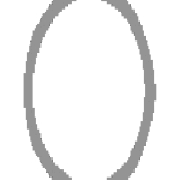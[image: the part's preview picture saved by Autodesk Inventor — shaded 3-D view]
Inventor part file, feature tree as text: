
AUTODESK INVENTOR PART (.ipt)
format: ipt  version: 2021 (Build 250183000, 183)  size: 112,128 bytes
history: native  units: in
note: dims shown in document units (in); Inventor stores cm internally (conversion verified against a paired STEP export)
features: other x4, sketch x3, plane x1
ambient origin geometry x8: Origin, YZ Plane, XZ Plane, XY Plane, X Axis, Y Axis, Z Axis, Center Point
bodies: Solid1 (feature_tree), Body (feature_tree)
feature tree (8):
  other  "Driven Length"
  other  "Frame Generator"
  other  "Start Plane"
  other  "End Plane"
  sketch  "Sketch"  dims[d2=28.9in d4=-0.0in d5=28.9in d6=0.12in d7=0.0in d8=90.0deg d9=28.9in]
  sketch  "Sketch2"  dims[d0=1.0in]
  plane  "Work Plane3"
  sketch  "Sketch3"  dims[d1=0.065in]
